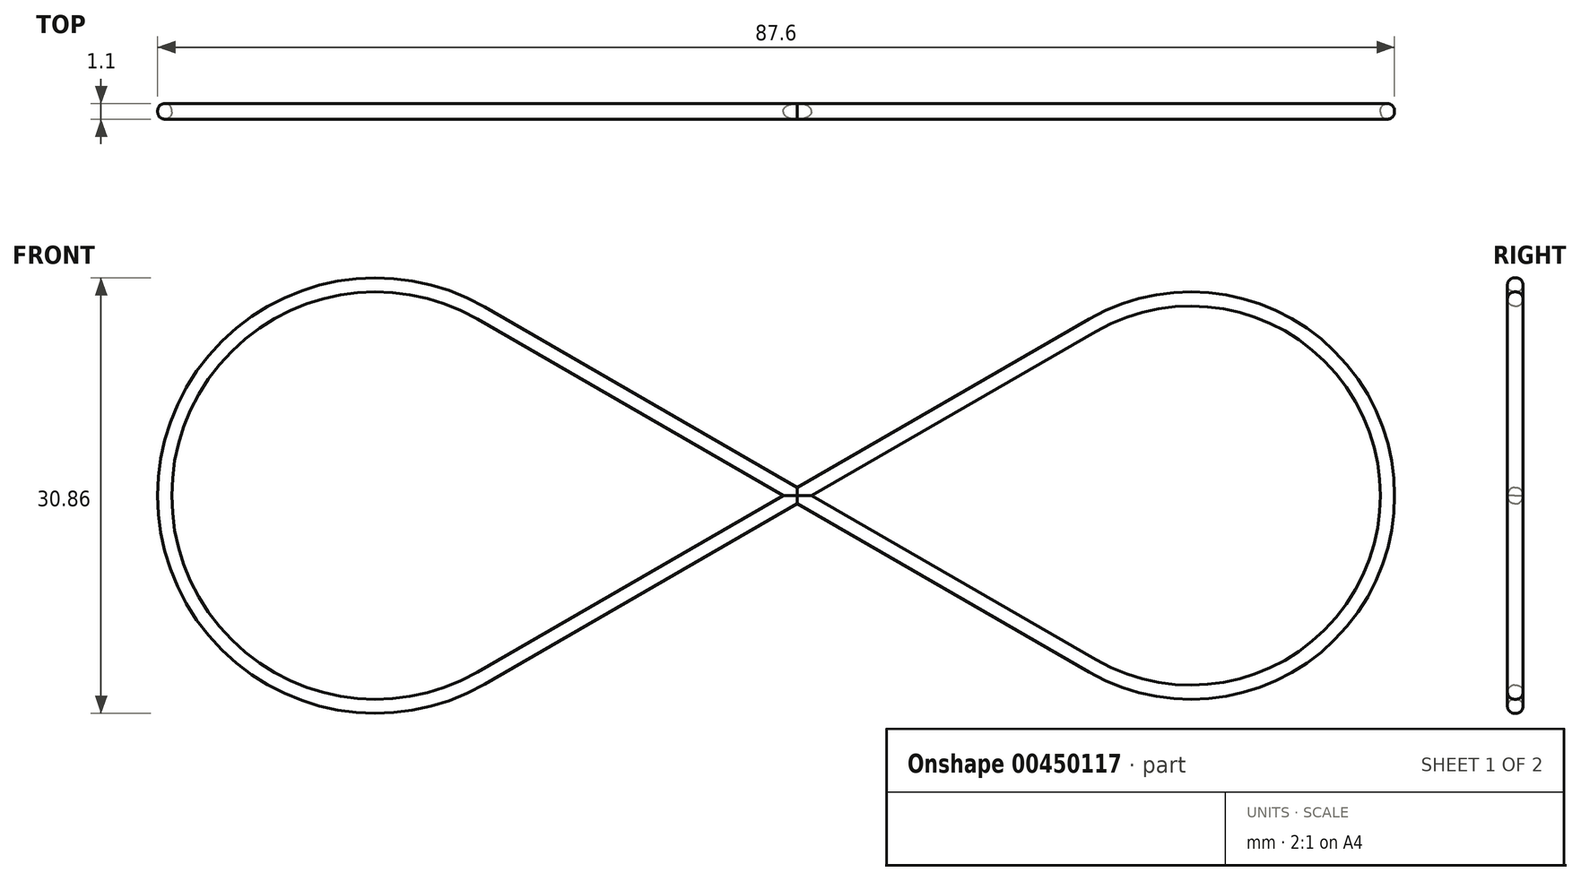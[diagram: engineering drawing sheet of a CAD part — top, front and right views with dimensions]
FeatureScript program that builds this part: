
annotation { "Feature Type Name" : "Feature", "Feature Type Description" : "" }
export const myFeature = defineFeature(function(context is Context, id is Id, definition is map)
    precondition{}
    {
        {
            var Q0;
            Q0=qCreatedBy(makeId("Front.planeOp"),FACE);
            var sketch = newSketch(context, id + "F0", { "sketchPlane" : qUnion([Q0])});
            skLineSegment(sketch, "E0", {"start": v(-25, 0) * mm, "end": v(25, 0) * mm, "construction": true});
            skLineSegment(sketch, "E1", {"start": v(0, -25) * mm, "end": v(0, 25) * mm, "construction": true});
            skCircle(sketch, "E2", {"center": v(0, 0) * mm, "radius": 25 * mm, "construction": true});
            skPoint(sketch, "E3.orphan", {"position": v(-43.48, 0) * mm});
            skPoint(sketch, "E4.orphan", {"position": v(0, -25.94) * mm});
            skLineSegment(sketch, "E5", {"start": v(-21.65, -12.5) * mm, "end": v(21.65, 12.5) * mm});
            skLineSegment(sketch, "E6.MirrorCS", {"start": v(-21.65, 12.5) * mm, "end": v(21.65, -12.5) * mm});
            skArc(sketch, "E7", {"start": v(21.65, -12.5) * mm, "mid": v(43.3, 0) * mm, "end": v(21.65, 12.5) * mm});
            skArc(sketch, "E8", {"start": v(-21.65, 12.5) * mm, "mid": v(-43.3, 0) * mm, "end": v(-21.65, -12.5) * mm});
            skArc(sketch, "E9.0", {"start": v(22.15, -11.63) * mm, "mid": v(42.3, 0) * mm, "end": v(22.15, 11.63) * mm});
            skLineSegment(sketch, "E9.1", {"start": v(-21.15, 13.37) * mm, "end": v(22.15, -11.63) * mm});
            skLineSegment(sketch, "E10.0", {"start": v(-21.15, -13.37) * mm, "end": v(22.15, 11.63) * mm});
            skArc(sketch, "E10.1", {"start": v(-21.15, 13.37) * mm, "mid": v(-44.3, 0) * mm, "end": v(-21.15, -13.37) * mm});
            skSolve(sketch);
        }
        {
            var Q0;
            Q0=qSketchRegion(id+"F0",true);
            extrude(context, id + "F1", {"entities" : qUnion([Q0]), "endBound" : BoundingType.SYMMETRIC, "depth" : 1.1 * mm});
        }
        {
            var Q0;
            Q0=makeQuery(id+"F1.opExtrude","CAP_FACE",FACE,{"disambiguationData":[OSD([sQuery(id+"F0.wireOp",EDGE,"E5"),sQuery(id+"F0.wireOp",EDGE,"E6.MirrorCS"),sQuery(id+"F0.wireOp",EDGE,"E7"),sQuery(id+"F0.wireOp",EDGE,"E8"),sQuery(id+"F0.wireOp",EDGE,"E9.0"),sQuery(id+"F0.wireOp",EDGE,"E9.1"),sQuery(id+"F0.wireOp",EDGE,"E10.0"),sQuery(id+"F0.wireOp",EDGE,"E10.1")])],"isStart":false});
            var Q1;
            Q1=makeQuery(id+"F1.opExtrude","CAP_FACE",FACE,{"disambiguationData":[OSD([sQuery(id+"F0.wireOp",EDGE,"E5"),sQuery(id+"F0.wireOp",EDGE,"E6.MirrorCS"),sQuery(id+"F0.wireOp",EDGE,"E7"),sQuery(id+"F0.wireOp",EDGE,"E8"),sQuery(id+"F0.wireOp",EDGE,"E9.0"),sQuery(id+"F0.wireOp",EDGE,"E9.1"),sQuery(id+"F0.wireOp",EDGE,"E10.0"),sQuery(id+"F0.wireOp",EDGE,"E10.1")])],"isStart":true});
            fillet(context, id + "F2", {"entities" : qUnion([Q0, Q1]), "radius" : .5 * mm, "tangentPropagation" : true, "allowEdgeOverflow" : false});
        }
    });
